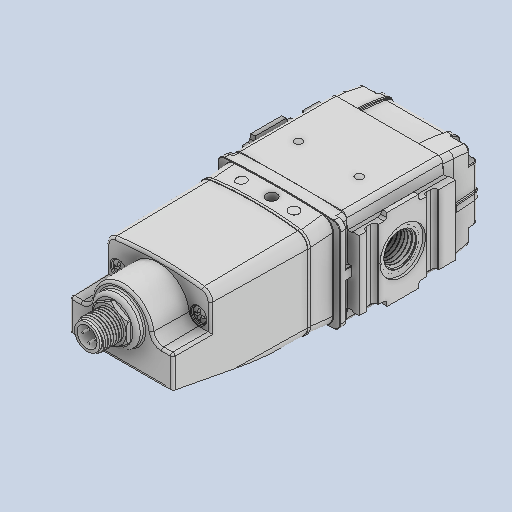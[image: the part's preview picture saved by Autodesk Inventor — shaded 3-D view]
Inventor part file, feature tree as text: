
AUTODESK INVENTOR PART (.ipt)
format: ipt  version: 2024.1 (Build 281209000, 209)  size: 3,846,144 bytes
history: native  units: in
note: dims shown in document units (in); Inventor stores cm internally (conversion verified against a paired STEP export)
features: other x53, fillet x3, mirror x1
ambient origin geometry x8: Origin, YZ Plane, XZ Plane, XY Plane, X Axis, Y Axis, Z Axis, Center Point
bodies: Solid1 (feature_tree), Solid2 (feature_tree), Solid3 (feature_tree), Solid4 (feature_tree), Solid5 (feature_tree), Solid6 (feature_tree), Solid7 (feature_tree), Solid8 (feature_tree), Solid9 (feature_tree), Solid10 (feature_tree), Solid11 (feature_tree), Solid12 (feature_tree), Solid13 (feature_tree), Solid14 (feature_tree), Solid15 (feature_tree), Solid16 (feature_tree), Solid17 (feature_tree), Solid18 (feature_tree), Solid19 (feature_tree), Solid20 (feature_tree), Solid21 (feature_tree), Solid22 (feature_tree), Solid23 (feature_tree), Solid24 (feature_tree), Solid25 (feature_tree), Solid26 (feature_tree), Solid27 (feature_tree), Solid28 (feature_tree), Solid29 (feature_tree), Solid30 (feature_tree), Solid31 (feature_tree), Solid32 (feature_tree), Solid33 (feature_tree), Solid34 (feature_tree), Solid35 (feature_tree), Solid36 (feature_tree), Solid37 (feature_tree), Solid38 (feature_tree), Solid39 (feature_tree), Solid40 (feature_tree), Solid41 (feature_tree), Solid42 (feature_tree), Solid43 (feature_tree), Solid44 (feature_tree), Solid45 (feature_tree), Solid46 (feature_tree), Solid47 (feature_tree), Solid48 (feature_tree), Solid49 (feature_tree), Solid50 (feature_tree), Solid51 (feature_tree), Solid52 (feature_tree), Solid53 (feature_tree), Solid54 (feature_tree), Solid55 (feature_tree), Solid56 (feature_tree), Solid57 (feature_tree)
feature tree (57):
  other  "Split1[1]"
  other  "Split3[1]"
  other  "Split3[2]"
  other  "Split4[1]"
  other  "Split4[2]"
  other  "Split4[3]"
  other  "Split4[4]"
  other  "Split5[1]"
  other  "Cut-Extrude3[1]"
  other  "Boss-Extrude2"
  other  "Boss-Extrude5"
  other  "Dome1"
  other  "CirPattern1[1]"
  other  "CirPattern1[2]"
  other  "CirPattern1[3]"
  other  "Split9[1]"
  other  "Split10[1]"
  other  "Cut-Sweep1"
  other  "Boss-Extrude9[1]"
  other  "Boss-Extrude9[2]"
  other  "Boss-Extrude9[3]"
  other  "Boss-Extrude9[4]"
  other  "Boss-Extrude9[5]"
  other  "Boss-Extrude9[6]"
  other  "Boss-Extrude9[7]"
  other  "Boss-Extrude9[8]"
  other  "Boss-Extrude9[9]"
  other  "Boss-Extrude9[10]"
  other  "Boss-Extrude9[11]"
  other  "Boss-Extrude9[12]"
  other  "Boss-Extrude9[13]"
  other  "Boss-Extrude9[14]"
  other  "Boss-Extrude9[15]"
  other  "Boss-Extrude9[16]"
  other  "Boss-Extrude9[17]"
  other  "Boss-Extrude9[18]"
  other  "Boss-Extrude9[19]"
  other  "Boss-Extrude9[20]"
  other  "Boss-Extrude9[21]"
  other  "Boss-Extrude9[22]"
  other  "Boss-Extrude9[23]"
  other  "Boss-Extrude9[24]"
  other  "Boss-Extrude9[25]"
  other  "Cut-Extrude7"
  fillet  "Fillet1"  [1 undecoded]
  fillet  "Fillet3"  [1 undecoded]
  fillet  "Fillet2"  [1 undecoded]
  other  "Boss-Extrude12"
  other  "Boss-Extrude13[1]"
  other  "Boss-Extrude13[2]"
  other  "Boss-Extrude13[3]"
  other  "Cut-Extrude10"
  other  "Boss-Extrude14[1]"
  other  "Boss-Extrude14[2]"
  other  "Dome2"
  mirror  "Mirror1"
  other  "Cut-Extrude-Thin3"
note: 3 required parameter values undecoded (feature->parameter linkage not recoverable at this tier; creation-order binding heuristic only, values carry confidence <= 0.55)
